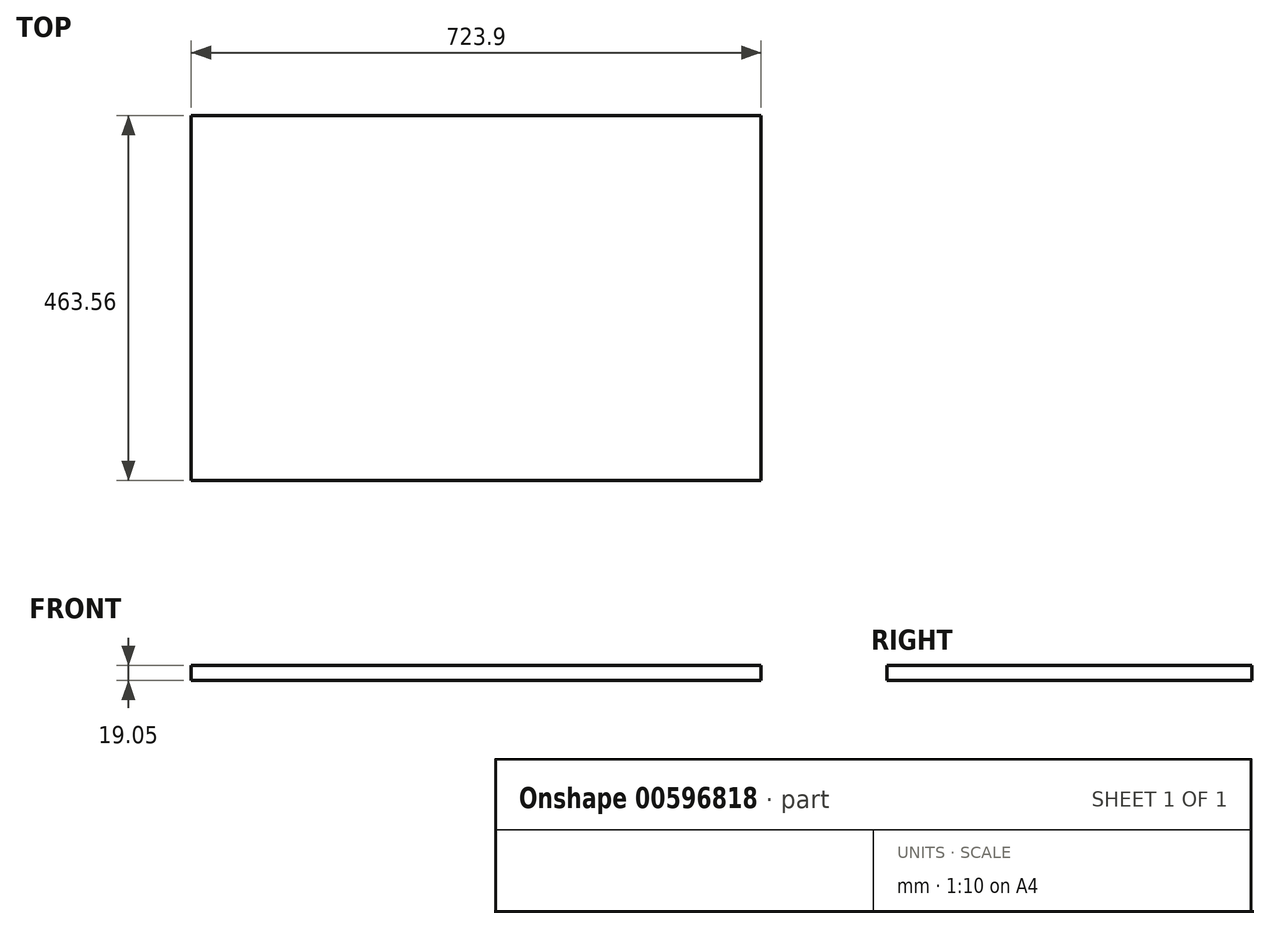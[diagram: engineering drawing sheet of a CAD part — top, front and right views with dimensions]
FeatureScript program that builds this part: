
annotation { "Feature Type Name" : "Feature", "Feature Type Description" : "" }
export const myFeature = defineFeature(function(context is Context, id is Id, definition is map)
    precondition{}
    {
        {
            var Q0;
            Q0=qCreatedBy(makeId("Top.planeOp"),FACE);
            var sketch = newSketch(context, id + "F0", { "sketchPlane" : qUnion([Q0])});
            skLineSegment(sketch, "E0.bottom", {"start": v(361.95, 231.77) * mm, "end": v(-361.95, 231.77) * mm});
            skLineSegment(sketch, "E0.top", {"start": v(361.95, -231.78) * mm, "end": v(-361.95, -231.78) * mm});
            skLineSegment(sketch, "E0.left", {"start": v(361.95, 231.77) * mm, "end": v(361.95, -231.78) * mm});
            skLineSegment(sketch, "E0.right", {"start": v(-361.95, 231.77) * mm, "end": v(-361.95, -231.78) * mm});
            skPoint(sketch, "E0.middle", {"position": v(0, 0) * mm});
            skSolve(sketch);
        }
        {
            var Q0;
            Q0=makeQuery(id+"F0.imprint","IMPRINT",FACE,{"disambiguationData":[TD([[makeQuery(id+"F0.imprint","IMPRINT",EDGE,{"derivedFrom":sQuery(id+"F0.wireOp",EDGE,"E0.bottom")}),1.0]])]});
            extrude(context, id + "F1", {"entities" : qUnion([Q0]), "depth" : 19.05 * mm, "offsetDistance" : 25.4 * mm});
        }
    });
